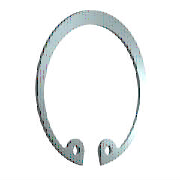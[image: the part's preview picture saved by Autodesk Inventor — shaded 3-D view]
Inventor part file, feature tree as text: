
AUTODESK INVENTOR PART (.ipt)
format: ipt  version: 2020 (Build 240168000, 168)  size: 152,064 bytes
history: native  units: mm (DEFAULTED — no unit token found)
features: other x2, extrude x1, plane x1
ambient origin geometry x8: Origin, YZ Plane, XZ Plane, XY Plane, X Axis, Y Axis, Z Axis, Center Point
bodies: Solid1 (feature_tree)
feature tree (4):
  extrude  "Bryła"  Depth=1.2mm
  other  "Work Axis1"
  other  "Work Axis2"
  plane  "Work Plane1"
